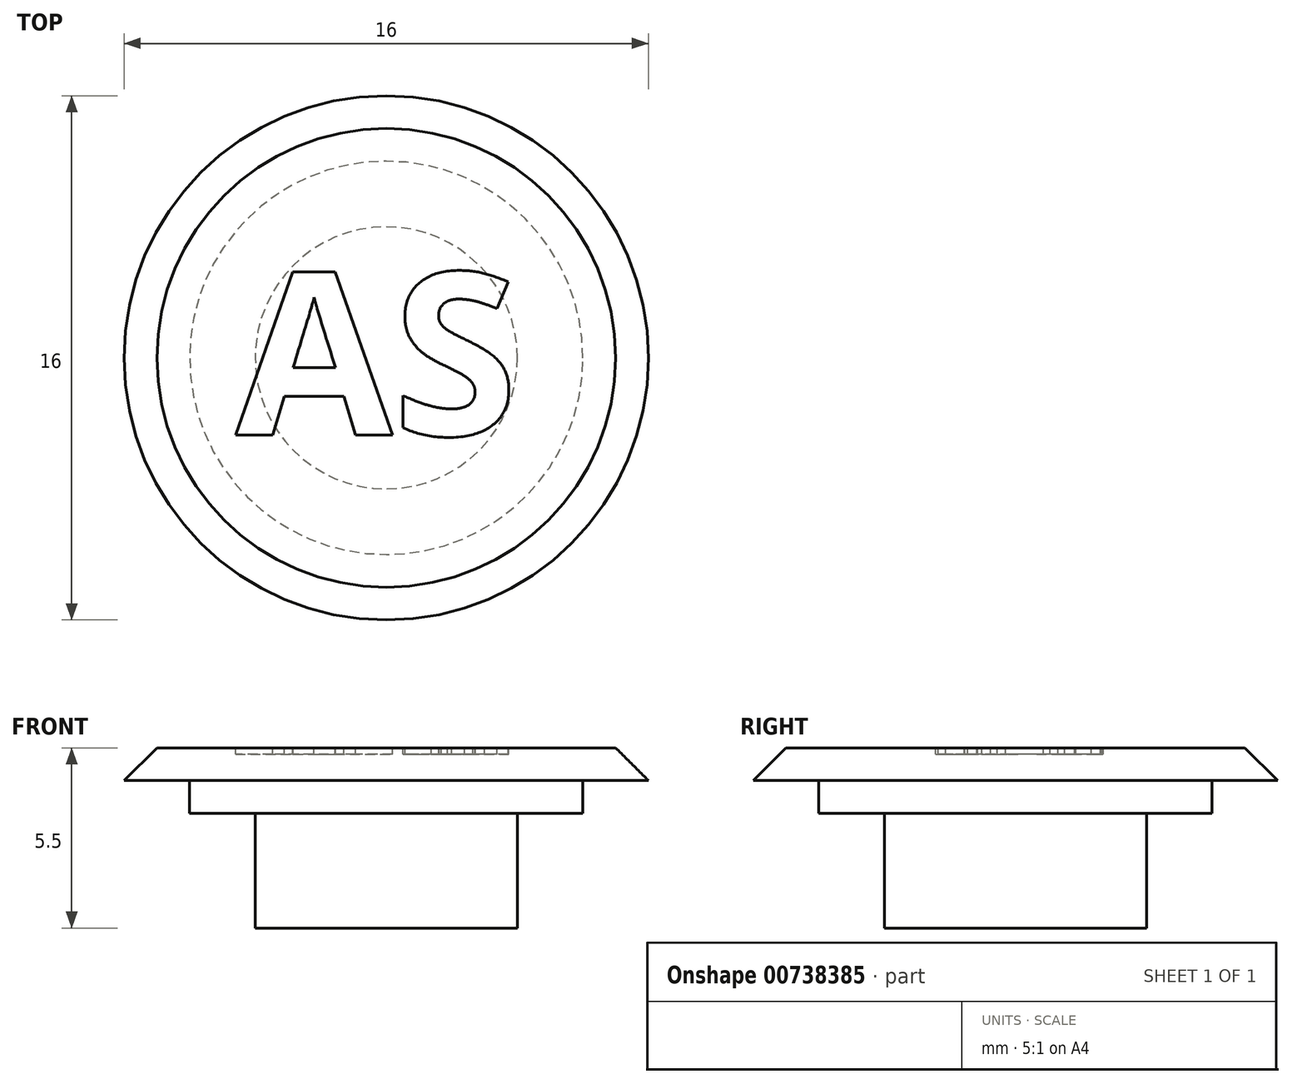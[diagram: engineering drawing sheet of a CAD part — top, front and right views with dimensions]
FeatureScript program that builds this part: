
annotation { "Feature Type Name" : "Feature", "Feature Type Description" : "" }
export const myFeature = defineFeature(function(context is Context, id is Id, definition is map)
    precondition{}
    {
        {
            var Q0;
            Q0=qCreatedBy(makeId("Top.planeOp"),FACE);
            var sketch = newSketch(context, id + "F0", { "sketchPlane" : qUnion([Q0])});
            skCircle(sketch, "E0", {"center": v(0, 0) * mm, "radius": 4 * mm});
            skSolve(sketch);
        }
        {
            var Q0;
            Q0=makeQuery(id+"F0.imprint","IMPRINT",FACE,{"disambiguationData":[TD([[makeQuery(id+"F0.imprint","IMPRINT",EDGE,{"derivedFrom":sQuery(id+"F0.wireOp",EDGE,"E0")}),1.0]])]});
            extrude(context, id + "F1", {"entities" : qUnion([Q0]), "depth" : 3.5 * mm, "offsetDistance" : 25 * mm});
        }
        {
            var Q0;
            Q0=makeQuery(id+"F1.opExtrude","CAP_FACE",FACE,{"disambiguationData":[OSD([sQuery(id+"F0.wireOp",EDGE,"E0")])],"isStart":false});
            var sketch = newSketch(context, id + "F2", { "sketchPlane" : qUnion([Q0])});
            skCircle(sketch, "E1", {"center": v(0, 0) * mm, "radius": 6 * mm});
            skSolve(sketch);
        }
        {
            var Q0;
            Q0=qSketchRegion(id+"F2",true);
            extrude(context, id + "F3", {"entities" : qUnion([Q0]), "operationType" : NewBodyOperationType.ADD, "depth" : 1 * mm, "offsetDistance" : 25 * mm});
        }
        {
            var Q0;
            Q0=makeQuery(id+"F3.opExtrude","CAP_FACE",FACE,{"disambiguationData":[OSD([sQuery(id+"F2.wireOp",EDGE,"E1")])],"isStart":false});
            var sketch = newSketch(context, id + "F4", { "sketchPlane" : qUnion([Q0])});
            skCircle(sketch, "E2", {"center": v(0, 0) * mm, "radius": 8 * mm});
            skSolve(sketch);
        }
        {
            var Q0;
            Q0=qSketchRegion(id+"F4",true);
            extrude(context, id + "F5", {"entities" : qUnion([Q0]), "operationType" : NewBodyOperationType.ADD, "depth" : 1 * mm, "offsetDistance" : 25 * mm});
        }
        {
            var Q0;
            Q0=makeQuery(id+"F5.opExtrude","CAP_FACE",FACE,{"disambiguationData":[OSD([sQuery(id+"F4.wireOp",EDGE,"E2")])],"isStart":false});
            var sketch = newSketch(context, id + "F6", { "sketchPlane" : qUnion([Q0])});
            skText(sketch, "E3", { "text": "AS", "fontName": "NotoSans-Bold.ttf"});
            const initialGuessF6  = {"E3": [-0.0046, -0.00236, 1, 0, 0.005]};
            skSetInitialGuess(sketch, initialGuessF6);
            skSolve(sketch);
        }
        {
            var Q0;
            Q0=makeQuery(id+"F6.imprint","IMPRINT",FACE,{"disambiguationData":[TD([[makeQuery(id+"F6.imprint","IMPRINT",EDGE,{"derivedFrom":sQuery(id+"F6.wireOp",EDGE,"E3.sketch_text.stroke-0")}),-1.0]])]});
            var Q1;
            Q1=makeQuery(id+"F6.imprint","IMPRINT",FACE,{"disambiguationData":[TD([[makeQuery(id+"F6.imprint","IMPRINT",EDGE,{"derivedFrom":sQuery(id+"F6.wireOp",EDGE,"E3.sketch_text.stroke-12")}),-1.0]])]});
            extrude(context, id + "F7", {"entities" : qUnion([Q0, Q1]), "operationType" : NewBodyOperationType.REMOVE, "oppositeDirection" : true, "depth" : 0.2 * mm, "offsetDistance" : 25 * mm});
        }
        {
            var Q0;
            Q0=makeQuery(id+"F5.opExtrude","CAP_EDGE",EDGE,{"disambiguationData":[OSD([sQuery(id+"F4.wireOp",EDGE,"E2")])],"isStart":false});
            chamfer(context, id + "F8", {"entities" : qUnion([Q0]), "width" : 1 * mm, "tangentPropagation" : true});
        }
    });
